# Revit family: Faucet-Counter_Mount-Kohler-Bancroft-10577_4X
name_source: partatom
category: Plumbing Fixtures
revit_build: Autodesk Revit MEP 2012 (Build: 20110916_2132(x64)
units: mm (PartAtom-declared; Revit-internal decimal feet)

## types (6) — shared parameters
Cold Water Flow = 0 GPM
Date Modified = March 13, 2015
Default Elevation = 48 "
Description = See Part Description
Equipment Abbreviation = WSF
Family Version = 1.0
Hot Water Flow = 0 GPM
Manufacturer = Kohler Company
Model = See Part Number
Model Disclaimer = Contact Kohler Company For More Information
Product Page URL = http://www.us.kohler.com
URL = http://www.us.kohler.com

## per-type parameters (varying)
| type | Product Material | zz Integer 2 |
| Polished Chrome | Chrome - Kohler - Polished | 1 |
| Vibrant Polished Nickel | Metal - Kohler - Vibrant Polished Nickel | 2 |
| Vibrant French Gold | Metal - Kohler - Vibrant French Gold | 3 |
| Vibrant Brushed Nickel | Metal - Kohler - Vibrant Brushed Nickel | 4 |
| Vibrant Brushed Bronze | Metal - Kohler - Vibrant Brushed Bronze | 5 |
| Oil-Rubbed Bronze | Metal - Kohler - Oil Rubbed Bronze | 6 |

## geometry (parser evidence)
native form markers: Blend x6, Sweep x1
no freeform markers — native parametric forms only
